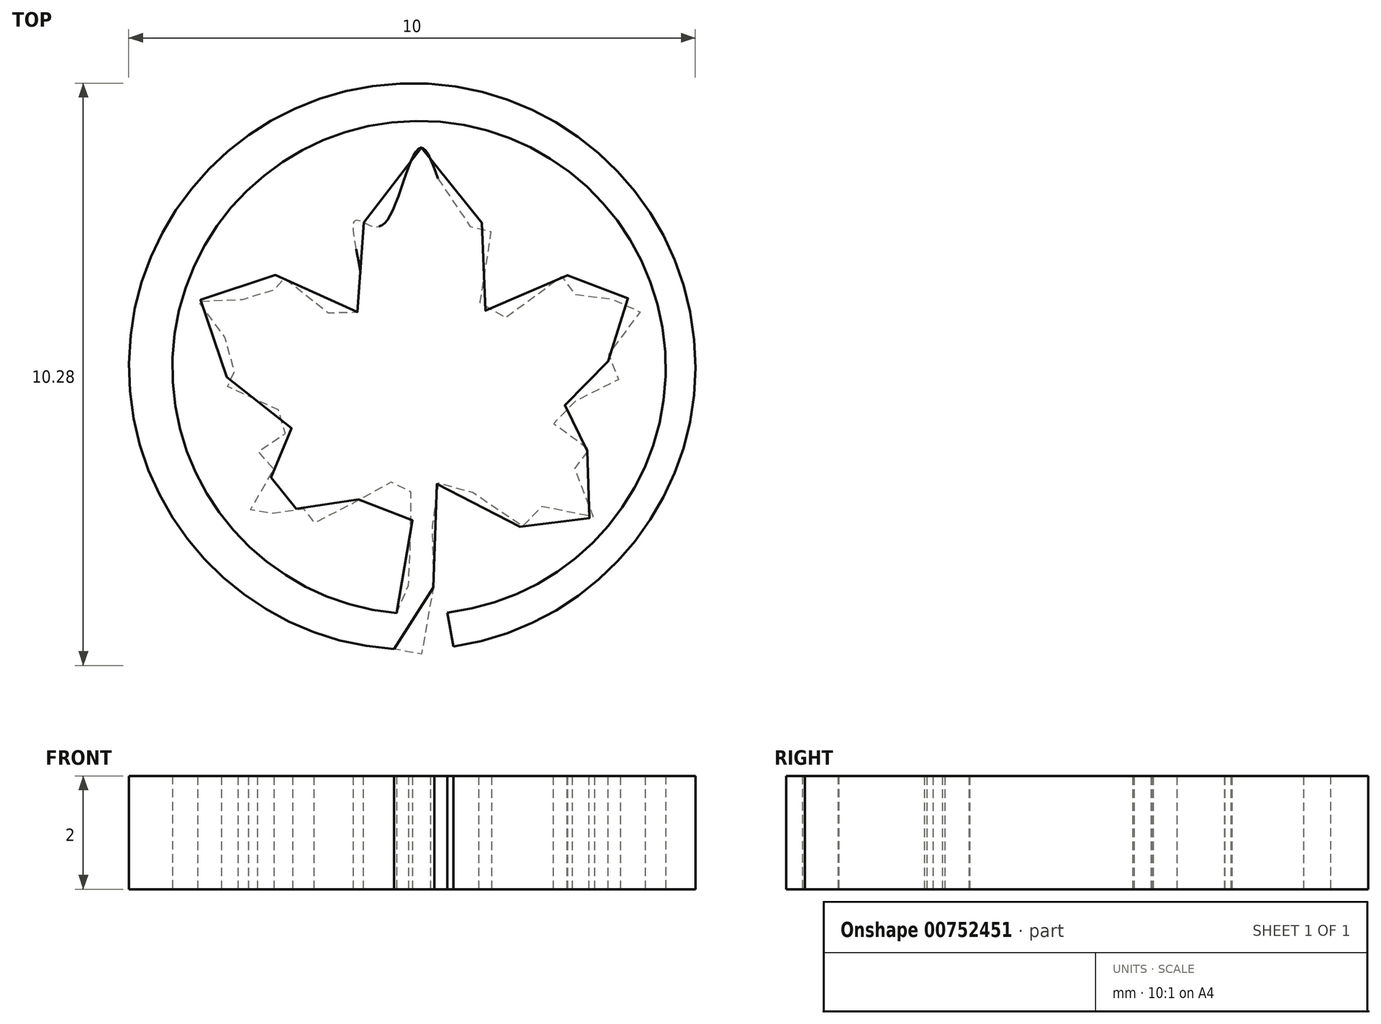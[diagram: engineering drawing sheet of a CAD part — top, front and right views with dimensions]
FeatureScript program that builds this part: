
annotation { "Feature Type Name" : "Feature", "Feature Type Description" : "" }
export const myFeature = defineFeature(function(context is Context, id is Id, definition is map)
    precondition{}
    {
        {
            var Q0;
            Q0=qCreatedBy(makeId("Top.planeOp"),FACE);
            var sketch = newSketch(context, id + "F0", { "sketchPlane" : qUnion([Q0])});
            skArc(sketch, "E0", {"start": v(-1.17, 2.7) * mm, "mid": v(-1.73, 11.37) * mm, "end": v(-2.07, 2.68) * mm});
            skArc(sketch, "E1", {"start": v(-1.07, 2.1) * mm, "mid": v(-2, 12.03) * mm, "end": v(-2.11, 2.05) * mm});
            skFitSpline(sketch, "E2", {"points": [v(-2.07, 2.68) * mm, v(-1.87, 3.11) * mm, v(-1.85, 3.55) * mm, v(-1.84, 4.9) * mm, v(-2.07, 5) * mm, v(-2.42, 4.9) * mm, v(-3.5, 4.26) * mm, v(-3.53, 4.45) * mm, v(-3.7, 4.52) * mm, v(-4.06, 4.5) * mm, v(-4.68, 4.39) * mm, v(-4.26, 5.14) * mm, v(-4.34, 5.46) * mm, v(-4.53, 5.57) * mm, v(-3.94, 5.94) * mm, v(-4.11, 6.24) * mm, v(-5.16, 6.77) * mm, v(-4.98, 6.9) * mm, v(-4.92, 7.3) * mm, v(-5.57, 8.18) * mm, v(-4.61, 8.22) * mm, v(-4.24, 8.38) * mm, v(-4.2, 8.67) * mm, v(-3.3, 8) * mm, v(-2.83, 7.96) * mm, v(-2.66, 8.28) * mm, v(-2.81, 9.6) * mm, v(-2.54, 9.53) * mm, v(-2.21, 9.66) * mm, v(-1.64, 10.9) * mm, v(-1.1, 9.8) * mm, v(-0.66, 9.53) * mm, v(-0.4, 9.63) * mm, v(-0.62, 8.26) * mm, v(-0.42, 7.97) * mm, v(-0.12, 7.91) * mm, v(0.93, 8.67) * mm, v(0.94, 8.46) * mm, v(1.15, 8.27) * mm, v(1.47, 8.2) * mm, v(2.32, 8.19) * mm, v(1.8, 7.54) * mm, v(1.66, 7.1) * mm, v(1.72, 6.9) * mm, v(1.88, 6.75) * mm, v(0.83, 6.32) * mm, v(0.71, 6.15) * mm, v(0.75, 5.95) * mm, v(1.32, 5.58) * mm, v(1.1, 5.48) * mm, v(1.07, 5.23) * mm, v(1.41, 4.4) * mm, v(0.6, 4.54) * mm, v(0.29, 4.5) * mm, v(0.16, 4.21) * mm, v(-0.8, 4.86) * mm, v(-1.2, 5.01) * mm, v(-1.43, 4.9) * mm, v(-1.43, 4.02) * mm, v(-1.45, 2.87) * mm, v(-1.76, 1.77) * mm, v(-2.11, 2.05) * mm], "startDerivative": vector(16.43, 29.8) * mm, "endDerivative": vector(-25.22, 32.47) * mm});
            skLineSegment(sketch, "E3", {"start": v(-1.17, 2.7) * mm, "end": v(-1.07, 2.1) * mm});
            skSolve(sketch);
        }
        {
            var Q0;
            Q0=makeQuery(id+"F0.imprint","IMPRINT",FACE,{"disambiguationData":[TD([[makeQuery(id+"F0.imprint","IMPRINT",EDGE,{"derivedFrom":sQuery(id+"F0.wireOp",EDGE,"E0")}),-1.0]])]});
            extrude(context, id + "F1", {"entities" : qUnion([Q0]), "depth" : 2 * mm, "offsetDistance" : 25 * mm});
        }
    });
